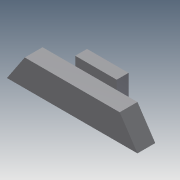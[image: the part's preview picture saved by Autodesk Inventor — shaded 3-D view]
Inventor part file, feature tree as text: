
AUTODESK INVENTOR PART (.ipt)
format: ipt  version: 2011 (Build 150239000, 239)  size: 120,320 bytes
history: native  units: in
note: dims shown in document units (in); Inventor stores cm internally (conversion verified against a paired STEP export)
features: extrude x5, sketch x5
ambient origin geometry x8: Origin, YZ Plane, XZ Plane, XY Plane, X Axis, Y Axis, Z Axis, Center Point
bodies: Solid1 (feature_tree)
feature tree (10):
  extrude  "Extrusion1"  Depth=2.25in
  extrude  "Extrusion2"  Depth=8.0in
  extrude  "Extrusion3"  Depth=0.75in
  extrude  "Extrusion4"  Depth=1.75in
  extrude  "Extrusion5"  Depth=3.5in
  sketch  "Sketch1"  dims[d0=11.0in d1=2.25in]
  sketch  "Sketch2"  dims[d2=4.0in d3=8.0in]
  sketch  "Sketch3"  dims[d4=1.5in d5=0.0in d6=0.75in]
  sketch  "Sketch4"  dims[d7=0.5in d8=0.0in d9=1.75in]
  sketch  "Sketch5"  dims[d10=1.375in d11=3.5in d12=2.75in d13=1.0in d14=0.0in d15=0.5in d16=0.5in d17=0.5in d18=0.75in d19=0.75in d20=2.5in d21=0.1in d22=0.0in d23=3.8583in d24=3.8583in d25=0.1875in d26=0.25in d27=0.0in]
